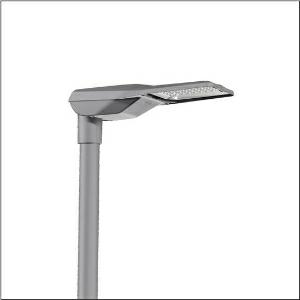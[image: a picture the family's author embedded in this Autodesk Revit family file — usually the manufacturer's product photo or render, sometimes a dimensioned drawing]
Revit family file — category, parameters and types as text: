
# Revit family: streetlight_sl_21_iq_mini___stw1_0a_5xe2e21d08hb_2a42
name_source: partatom
category: Lighting Fixtures
units: mm (PartAtom-declared; Revit-internal decimal feet)

## family parameters
Cut with Voids When Loaded = No
Host = Face
Light Source = No
Part Type = Normal
Room Calculation Point = No
Round Connector Dimension = Use Diameter
Shared = No

## types (1)
- --- (1 x LED, 7830 lm, 70.9 W, 2200K)
    Apparent Load = 71 VA
    CIE Flux Codes = 38 75 98 100 100
    Color Rendering = 70
    Color Temperature = 2200K
    Default Elevation = 1800 mm
    Description = Streetlight SL 21 iQ mini, mast luminaire, primary light control with lens, of PMMA, primary optical cover: cover, of toughened safety glass, transparent, light distribution: STW1.0a, light emission: direct distribution, primary light characteristic: asymmetric, installation type: post-top, side-entry, LED, High Power LED, rated luminous flux: 7.830lm, luminous efficacy: 110lm/W, light colour: 722, colour temperature: 2200K, control gear: iQ-Comfort, control: Auto-Match, Temp-Guard, Lumen-Switch, Night-Set, Smart-Wire, Light-Fading, Desk-Remote (wireless, voltage-free reading and setting of iQ features in the workshop via application-optimized NFC function/RFID function), optimised constant luminous flux control (CLO 2.0), pre-setting: linear dimming characteristic, mains connection: 220..240V, AC, 50/60Hz, start of lifetime: 71W, end of service life: 75W, reduction: 31W, luminaire housing, of diecast aluminium, powder-coated, SITECO metallic grey (DB 702S), corrosivity category C5 high according to DIN EN ISO 12944, please order mast flange separately, inclination adjustable: 0°, 5°, 10°, 15°, sealing non-destructively replaceable, multi-level sealing system, length: 628mm, width: 235mm, height: 110mm, mast flange for spigot size: 42mm (side-entry): 5XC10008XM4, 60/48mm (side-entry/post-top): 5XC10108XM2, 76/60mm (side-entry/post-top): 5XC10108XM1, mounting height: 4..8m, protection rating (complete): IP66, insulation class (complete): insulation class II (safety insulation), certification: CE, ENEC, ENEC+, VDE, impact resistance: IK10, permissible operating ambient temperature for outdoor applications: -40..+50°C, standard-compliant lighting for roads and squares, packaging unit: 1 piece

Light Distribution: STW1.0a
    Height = 110 mm
    Lamp = 1 x LED
    Lamp Light Flux = 7830 lm
    Lamp Power = 70.9 W
    Lamp count = 1
    Length = 625 mm
    Luminous efficacy = 110 lm/W
    Manufacturer = Siteco
    ModVariant = No
    Model = 5XE2E21D08HB
    Number of Poles = 1
    OnlyDefault = Yes
    Power Factor = 1
    Product Name = Streetlight SL 21 iQ mini | STW1.0a
    Product group = mast luminaire | pylon top
    ProductGroupID = 6100
    Protection Class = Protection class II
    Protection Degree = IP 66
    RLX_Detail_Level = 1
    RLX_Emergency_Light_Flux = 0 lm
    RLX_Emergency_Type = 0
    RLX_Emergency_Type_DB = No
    RlxData = <blob elided: 26309 chars, md5=f136ff8d>
    Socket = socket
    Standby Power = 0 W
    System Light Flux = 7830 lm
    System Power = 71 W
    Type Comments = factory setting: luminous flux: 100 % | dim-lin: 254 | 711 mA
    Type Image = l_1003519.jpg
    URL = http://relux.com
    VarID = @adj_157489
    Voltage = 0 V
    Weight = 0.00 kg
    Width = 234 mm

## geometry (parser evidence)
native form markers: Blend x4, Sweep x10
no freeform markers — native parametric forms only
